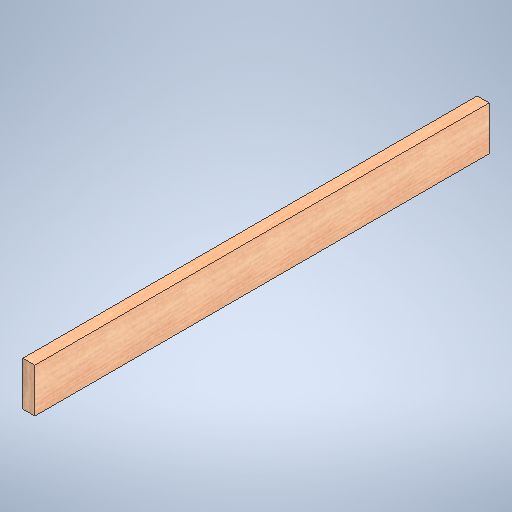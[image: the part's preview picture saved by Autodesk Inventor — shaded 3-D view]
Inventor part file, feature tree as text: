
AUTODESK INVENTOR PART (.ipt)
format: ipt  version: 2025 (Build 290162010, 162A)  size: 310,784 bytes
history: native  units: in
note: dims shown in document units (in); Inventor stores cm internally (conversion verified against a paired STEP export)
features: extrude x1, sketch x1
ambient origin geometry x8: Origin, YZ Plane, XZ Plane, XY Plane, X Axis, Y Axis, Z Axis, Center Point
bodies: Solid1 (feature_tree)
feature tree (2):
  extrude  "Extrusion1"  Depth=5.5in
  sketch  "Sketch1"  dims[d0=1.5in d1=5.5in d2=56.75in d3=0.0in]
